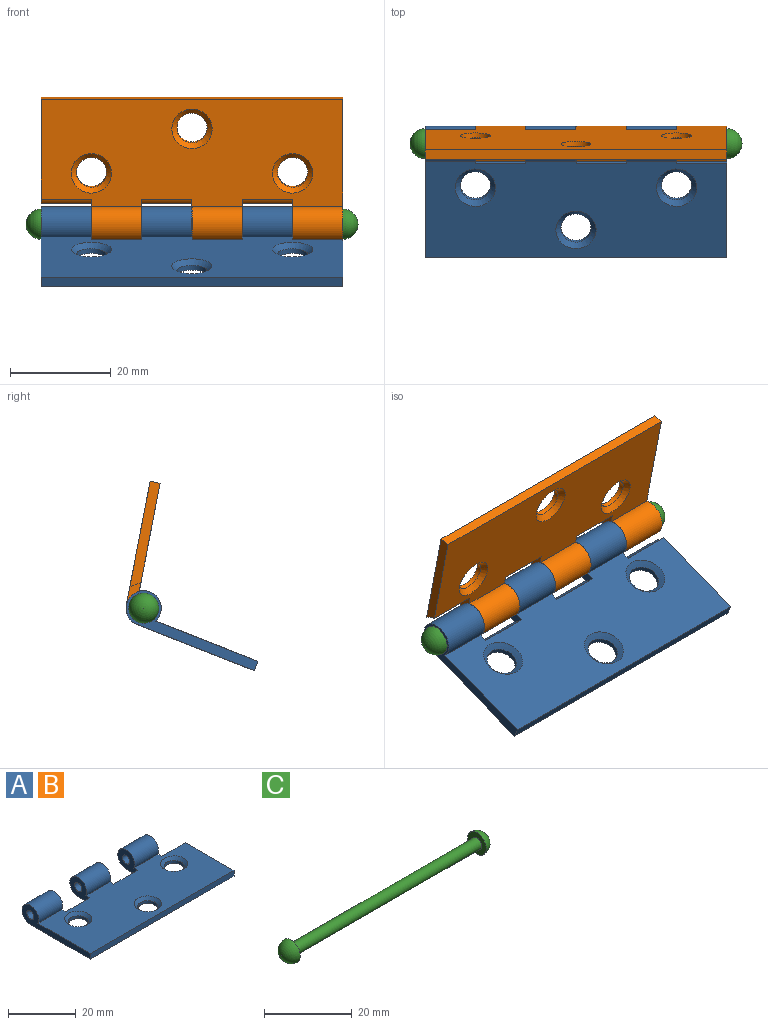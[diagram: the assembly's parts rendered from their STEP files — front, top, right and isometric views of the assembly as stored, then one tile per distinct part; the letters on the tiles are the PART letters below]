
ASSEMBLY  parts=3 mates=2
PART A: 25 faces, bbox 60x28.5x7 mm
  f0: cylinder r=3.5mm len=10mm, axis (-1,0,0), area 180.4mm2, adj f2,f3,f10,f23
  f1: cylinder r=1.5mm len=10mm, axis (-1,0,0), area 94.2mm2, adj f10,f23
  f2: plane 60x21.84mm, normal (0,0,1), area 1111.2mm2, adj f0,f4,f6,f8,f9,f10,f14,f15
  f3: plane 60x25mm, normal (0,0,-1), area 1308.1mm2, adj f0,f4,f6,f8,f9,f10,f11,f12
  f4: cylinder r=3.5mm len=10mm, axis (-1,0,0), area 180.4mm2, adj f2,f3,f20,f24
  f5: cylinder r=1.5mm len=10mm, axis (-1,0,0), area 94.2mm2, adj f20,f24
  f6: cylinder r=3.5mm len=10mm, axis (-1,0,0), area 180.4mm2, adj f2,f3,f18,f21
  f7: cylinder r=1.5mm len=10mm, axis (-1,0,0), area 94.2mm2, adj f18,f21
  f8: plane 60x2mm, normal (0,-1,0), area 120mm2, adj f2,f3,f9,f10
  f9: plane 21.43x2mm, normal (1,0,0), area 41.4mm2, adj f2,f3,f8,f17
  f10: plane 28.5x7mm, normal (-1,0,0), area 76.9mm2, adj f0,f1,f2,f3,f8
  f11: cylinder r=3mm len=6mm, axis (0,0,1), area 18.8mm2, adj f3,f15
  f12: cylinder r=3mm len=6mm, axis (0,0,1), area 18.8mm2, adj f3,f14
  f13: cylinder r=3mm len=6mm, axis (0,0,1), area 18.8mm2, adj f3,f16
  f14: cone r=3mm half-angle=45deg, axis (0,0,1), area 31.1mm2, adj f2,f12
  f15: cone r=3mm half-angle=45deg, axis (0,0,1), area 31.1mm2, adj f2,f11
  f16: cone r=3mm half-angle=45deg, axis (0,0,1), area 31.1mm2, adj f2,f13
  f17: cylinder r=5mm len=10mm, axis (1,0,0), area 23.5mm2, adj f2,f3,f9,f18
  f18: plane 8.27x7mm, normal (1,0,0), area 35.4mm2, adj f2,f3,f6,f7,f17
  f19: cylinder r=5mm len=10mm, axis (1,0,0), area 23.5mm2, adj f2,f3,f20,f21
  f20: plane 8.27x7mm, normal (1,0,0), area 35.4mm2, adj f2,f3,f4,f5,f19
  f21: plane 8.27x7mm, normal (-1,0,0), area 35.4mm2, adj f2,f3,f6,f7,f19
  f22: cylinder r=5mm len=10mm, axis (1,0,0), area 23.5mm2, adj f2,f3,f23,f24
  f23: plane 8.27x7mm, normal (1,0,0), area 35.4mm2, adj f0,f1,f2,f3,f22
  f24: plane 8.27x7mm, normal (-1,0,0), area 35.4mm2, adj f2,f3,f4,f5,f22
PART B: same geometry as A
PART C: 5 faces, bbox 66x6x6 mm
  f0: cylinder r=1.5mm len=60mm, axis (-1,0,0), area 565.5mm2, adj f2,f4
  f1: sphere r=3mm, area 56.5mm2, adj f2
  f2: plane 6x6mm, normal (-1,0,0), area 21.2mm2, adj f0,f1
  f3: sphere r=3mm, area 56.5mm2, adj f4
  f4: plane 6x6mm, normal (1,0,0), area 21.2mm2, adj f0,f3
PLACE A rot(axis=(1,0,0),21.5deg) t=(-3.45,2.55,2.14)mm fixed
PLACE B rot(axis=(0,0.77,-0.64),180deg) t=(56.55,2.55,2.14)mm
PLACE C rot(axis=(1,0,0),21.5deg) t=(26.55,2.55,2.14)mm
MATE fastened C.f0 <-> A.f0  axis (-1,0,0) through (-3.45,2.55,2.14)mm
MATE revolute B.f0 <-> A.f0  axis (-1,0,0) through (46.55,2.55,2.14)mm
